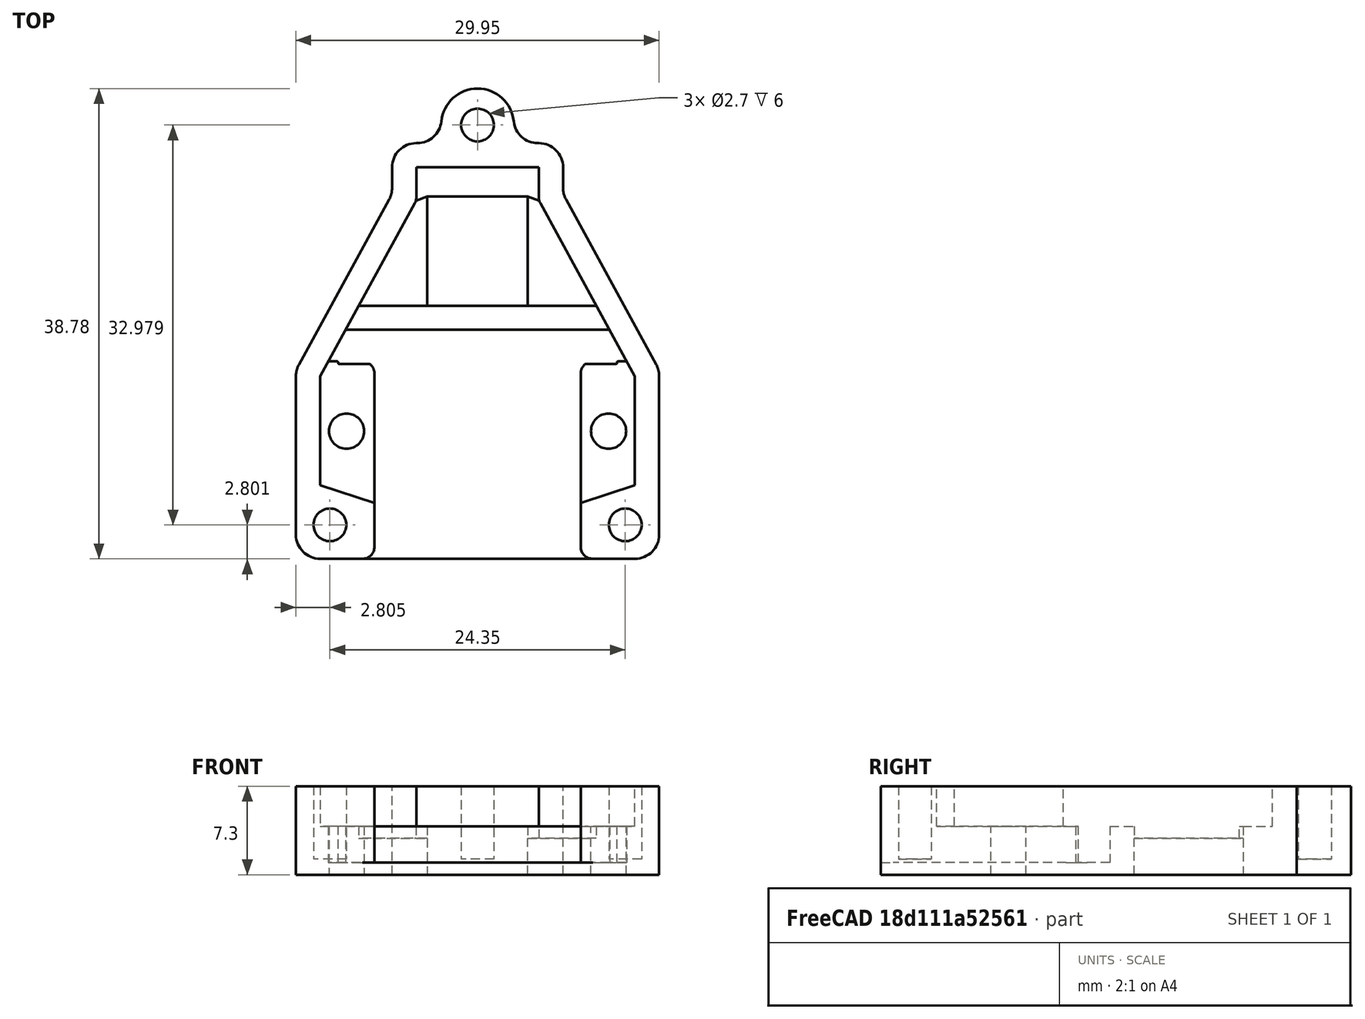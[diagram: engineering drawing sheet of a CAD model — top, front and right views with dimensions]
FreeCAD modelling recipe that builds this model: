
FCSTD DOCUMENT  (FreeCAD 0.14R3692 (Git))
Label: InkjetHolderHorizontalMount
License: CC-BY 3.0
LicenseURL: http://creativecommons.org/licenses/by/3.0/
objects: Part::Fillet×6, Part::Feature×1, Part::Box×1, Part::Cut×1
note: 9 computed .brp shape members not serialized (recipe doc carries the construction recipe); baked Part::Feature solids carry a one-line shape summary decoded from their .brp

FEATURE [Part::Feature] Part__Feature  label="InkjetHolderHorizontalMount1"
  shape: bbox 29.95 x 38.78 x 7.3 mm, 65 faces (baked)
FEATURE [Part::Box] Box  label="Cube"
  Height = 10
  Length = 23
  Placement = pos=(-11.5,9.8,-6) rot=(0,0,1;0rad)
  Width = 1
FEATURE [Part::Cut] Cut
  Base = -> Part__Feature
  Tool = -> Box
FEATURE [Part::Fillet] Fillet
  Base = -> Cut
  Edges = 1 edges r=0.07: [Edge162]
FEATURE [Part::Fillet] Fillet001
  Base = -> Fillet
  Edges = 1 edges r=0.07: [Edge25]
FEATURE [Part::Fillet] Fillet002
  Base = -> Fillet001
  Edges = 1 edges r=0.2: [Edge21]
FEATURE [Part::Fillet] Fillet003
  Base = -> Fillet002
  Edges = 1 edges r=0.07: [Edge196]
FEATURE [Part::Fillet] Fillet004
  Base = -> Fillet003
  Edges = 1 edges r=0.07: [Edge57]
FEATURE [Part::Fillet] Fillet005  label="InkjetHolderHorizontalMount"
  Base = -> Fillet004
  Edges = 1 edges r=0.2: [Edge15]
